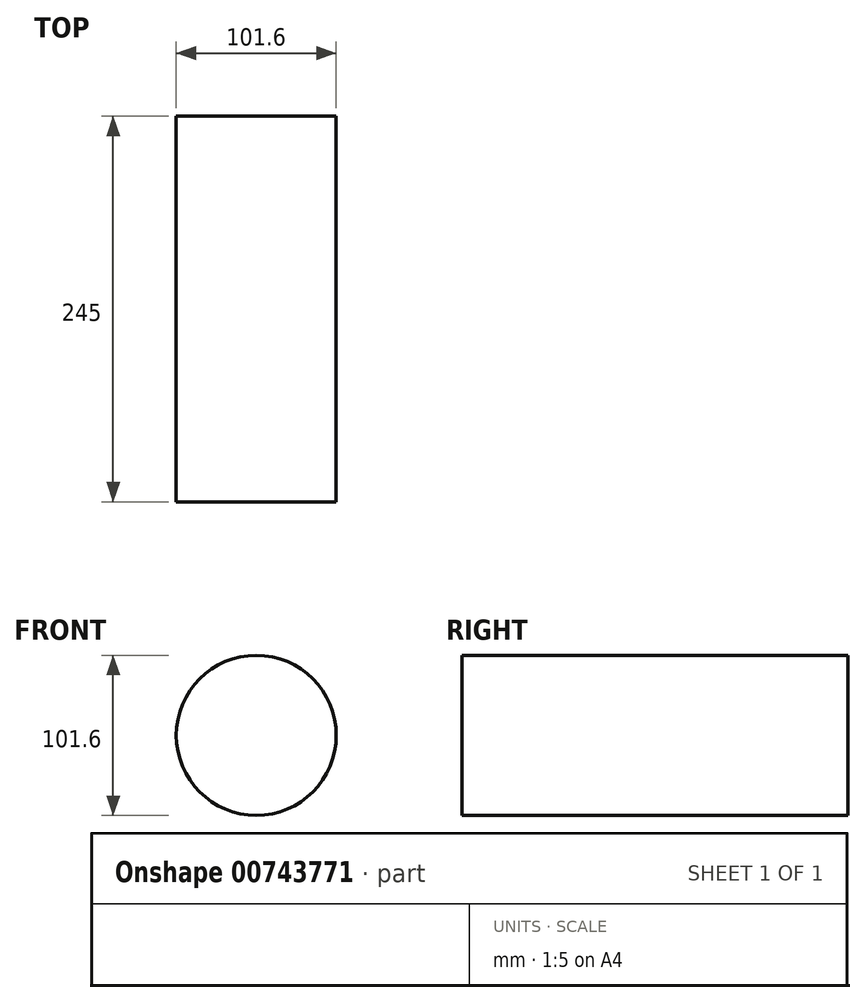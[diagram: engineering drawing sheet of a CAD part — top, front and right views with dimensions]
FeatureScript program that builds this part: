
annotation { "Feature Type Name" : "Feature", "Feature Type Description" : "" }
export const myFeature = defineFeature(function(context is Context, id is Id, definition is map)
    precondition{}
    {
        {
            var Q0;
            Q0=qCreatedBy(makeId("Front.planeOp"),FACE);
            var sketch = newSketch(context, id + "F0", { "sketchPlane" : qUnion([Q0])});
            skCircle(sketch, "E0", {"center": v(0, 0) * mm, "radius": 50.8 * mm});
            skSolve(sketch);
        }
        {
            var Q0;
            Q0 = qSketchRegion(id + "F0", true);
            extrude(context, id + "F1", {"entities" : qUnion([Q0]), "oppositeDirection" : true, "depth" : 245 * mm, "offsetDistance" : 25 * mm});
        }
    });
